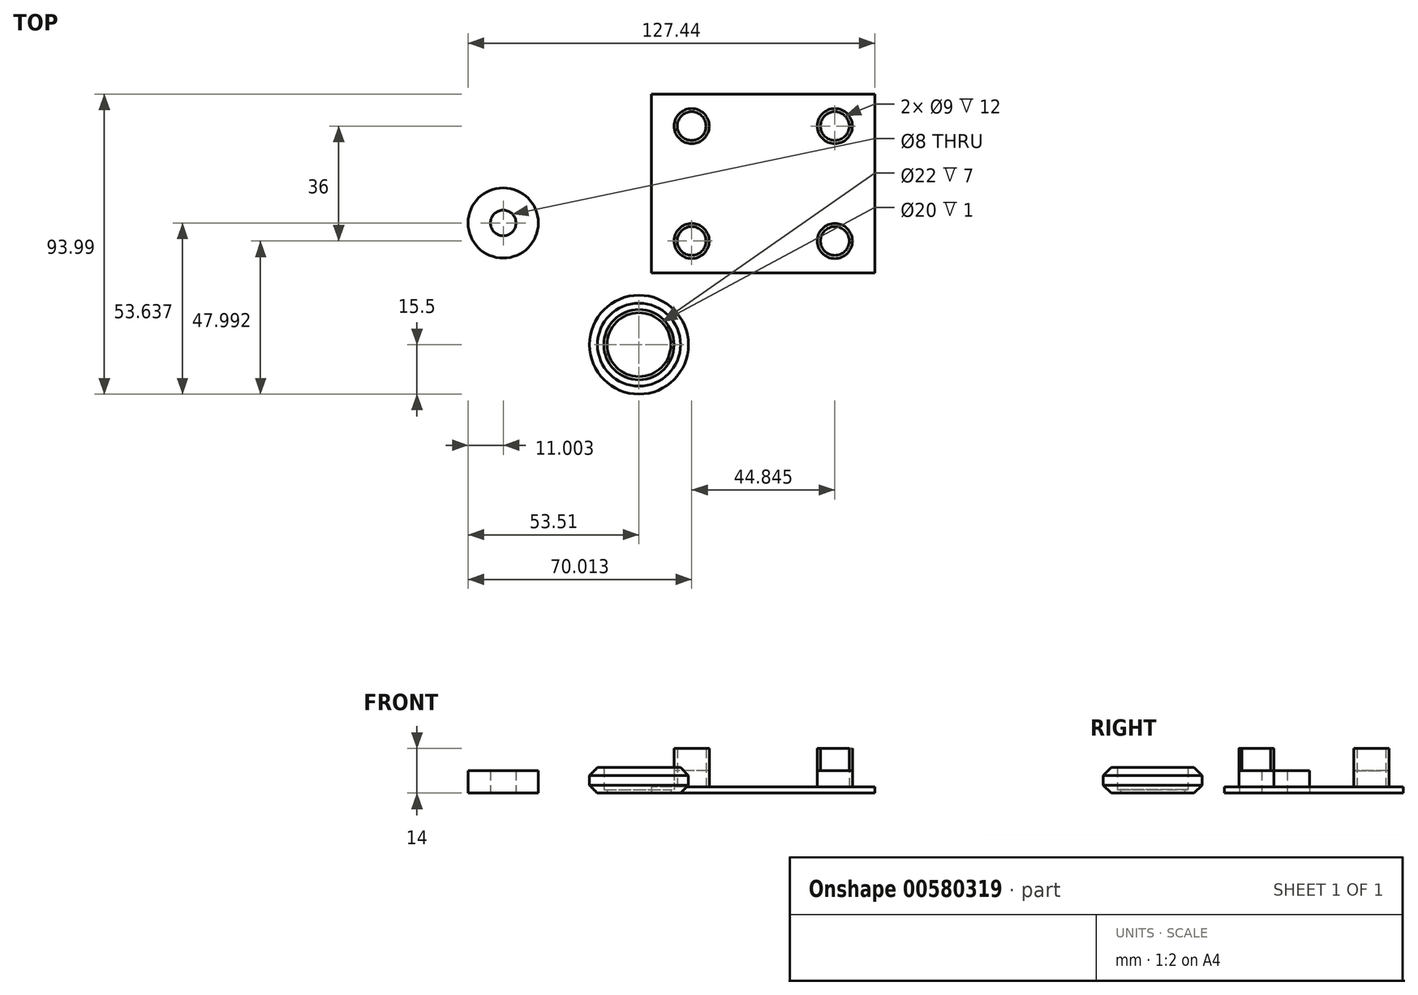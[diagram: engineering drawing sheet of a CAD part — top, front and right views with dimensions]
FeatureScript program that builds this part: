
annotation { "Feature Type Name" : "Feature", "Feature Type Description" : "" }
export const myFeature = defineFeature(function(context is Context, id is Id, definition is map)
    precondition{}
    {
        {
            var Q0;
            Q0=qCreatedBy(makeId("Right.planeOp"),FACE);
            var sketch = newSketch(context, id + "F0", { "sketchPlane" : qUnion([Q0])});
            skLineSegment(sketch, "E0", {"start": v(0, 0) * mm, "end": v(2, 0) * mm});
            skLineSegment(sketch, "E1", {"start": v(2, 0) * mm, "end": v(6, 4) * mm});
            skLineSegment(sketch, "E2", {"start": v(6, 4) * mm, "end": v(2, 8) * mm});
            skLineSegment(sketch, "E3", {"start": v(2, 8) * mm, "end": v(0, 8) * mm});
            skLineSegment(sketch, "E4", {"start": v(0, 8) * mm, "end": v(0, 0) * mm});
            skLineSegment(sketch, "E5", {"start": v(-11, 0) * mm, "end": v(-11, 5.99) * mm});
            skLineSegment(sketch, "E6.bottom", {"start": v(0, 1) * mm, "end": v(-1, 1) * mm});
            skLineSegment(sketch, "E6.top", {"start": v(0, 0) * mm, "end": v(-1, 0) * mm});
            skLineSegment(sketch, "E6.left", {"start": v(0, 1) * mm, "end": v(0, 0) * mm});
            skLineSegment(sketch, "E6.right", {"start": v(-1, 1) * mm, "end": v(-1, 0) * mm});
            skLineSegment(sketch, "E7", {"start": v(4.5, 5.5) * mm, "end": v(4.5, 2.5) * mm});
            skSolve(sketch);
        }
        {
            var Q0;
            {var subQ4=sQuery(id+"F0.wireOp",EDGE,"E0");Q0=makeQuery(id+"F0.imprint","IMPRINT",FACE,{"disambiguationData":[TD([[makeQuery(id+"F0.imprint","IMPRINT",EDGE,{"derivedFrom":subQ4}),1.0]])]});}
            var Q1;
            Q1=makeQuery(id+"F0.imprint","IMPRINT",FACE,{"disambiguationData":[TD([[makeQuery(id+"F0.imprint","IMPRINT",EDGE,{"derivedFrom":sQuery(id+"F0.wireOp",EDGE,"E6.bottom")}),1.0]])]});
            var Q2;
            Q2=sQuery(id+"F0.wireOp",EDGE,"E5");
            revolve(context, id + "F1", {"entities" : qUnion([Q0, Q1]), "axis" : qUnion([Q2]), "revolveType" : RevolveType.FULL});
        }
        {
            var Q0;
            Q0=qCreatedBy(makeId("Top.planeOp"),FACE);
            var sketch = newSketch(context, id + "F2", { "sketchPlane" : qUnion([Q0])});
            skCircle(sketch, "E8", {"center": v(-42.5, 27.14) * mm, "radius": 11 * mm});
            skCircle(sketch, "E9", {"center": v(-42.5, 27.14) * mm, "radius": 4 * mm});
            skSolve(sketch);
        }
        {
            var Q0;
            Q0=qSketchRegion(id+"F2",true);
            extrude(context, id + "F3", {"entities" : qUnion([Q0]), "depth" : 7 * mm});
        }
        {
            var Q0;
            Q0=qCreatedBy(makeId("Top.planeOp"),FACE);
            var sketch = newSketch(context, id + "F4", { "sketchPlane" : qUnion([Q0])});
            skLineSegment(sketch, "E10.bottom", {"start": v(73.93, 11.5) * mm, "end": v(3.93, 11.5) * mm});
            skLineSegment(sketch, "E10.top", {"start": v(73.93, 67.5) * mm, "end": v(3.93, 67.5) * mm});
            skLineSegment(sketch, "E10.left", {"start": v(73.93, 11.5) * mm, "end": v(73.93, 67.5) * mm});
            skLineSegment(sketch, "E10.right", {"start": v(3.93, 11.5) * mm, "end": v(3.93, 67.5) * mm});
            skSolve(sketch);
        }
        {
            var Q0;
            Q0=qSketchRegion(id+"F4",true);
            extrude(context, id + "F5", {"entities" : qUnion([Q0]), "depth" : 2 * mm});
        }
        {
            var Q0;
            Q0=makeQuery(id+"F5.opExtrude","CAP_FACE",FACE,{"disambiguationData":[OSD([sQuery(id+"F4.wireOp",EDGE,"E10.bottom"),sQuery(id+"F4.wireOp",EDGE,"E10.top"),sQuery(id+"F4.wireOp",EDGE,"E10.left"),sQuery(id+"F4.wireOp",EDGE,"E10.right")])],"isStart":false});
            var sketch = newSketch(context, id + "F6", { "sketchPlane" : qUnion([Q0])});
            skLineSegment(sketch, "E11", {"start": v(38.93, 11.5) * mm, "end": v(38.93, 67.5) * mm});
            skLineSegment(sketch, "E12", {"start": v(3.93, 39.5) * mm, "end": v(73.93, 39.5) * mm});
            skCircle(sketch, "E13", {"center": v(61.35, 21.5) * mm, "radius": 5.5 * mm});
            skCircle(sketch, "E14", {"center": v(61.35, 21.5) * mm, "radius": 4.5 * mm});
            skCircle(sketch, "E15.MirrorC", {"center": v(16.5, 21.5) * mm, "radius": 5.5 * mm});
            skCircle(sketch, "E16.MirrorC", {"center": v(16.5, 21.5) * mm, "radius": 4.5 * mm});
            skLineSegment(sketch, "E17.MirrorCS", {"start": v(73.93, 39.5) * mm, "end": v(3.93, 39.5) * mm});
            skCircle(sketch, "E18.MirrorC", {"center": v(61.35, 57.5) * mm, "radius": 4.5 * mm});
            skCircle(sketch, "E19.MirrorC", {"center": v(61.35, 57.5) * mm, "radius": 5.5 * mm});
            skCircle(sketch, "E20.MirrorC", {"center": v(16.5, 57.5) * mm, "radius": 5.5 * mm});
            skCircle(sketch, "E21.MirrorC", {"center": v(16.5, 57.5) * mm, "radius": 4.5 * mm});
            skSolve(sketch);
        }
        {
            var Q0;
            Q0=makeQuery(id+"F6.imprint","IMPRINT",FACE,{"disambiguationData":[TD([[makeQuery(id+"F6.imprint","IMPRINT",EDGE,{"derivedFrom":sQuery(id+"F6.wireOp",EDGE,"E14")}),1.0]])]});
            var Q1;
            Q1=makeQuery(id+"F6.imprint","IMPRINT",FACE,{"disambiguationData":[TD([[makeQuery(id+"F6.imprint","IMPRINT",EDGE,{"derivedFrom":sQuery(id+"F6.wireOp",EDGE,"E16.MirrorC")}),-1.0]])]});
            var Q2;
            Q2=makeQuery(id+"F6.imprint","IMPRINT",FACE,{"disambiguationData":[TD([[makeQuery(id+"F6.imprint","IMPRINT",EDGE,{"derivedFrom":sQuery(id+"F6.wireOp",EDGE,"E21.MirrorC")}),1.0]])]});
            var Q3;
            Q3=makeQuery(id+"F6.imprint","IMPRINT",FACE,{"disambiguationData":[TD([[makeQuery(id+"F6.imprint","IMPRINT",EDGE,{"derivedFrom":sQuery(id+"F6.wireOp",EDGE,"E18.MirrorC")}),-1.0]])]});
            extrude(context, id + "F7", {"entities" : qUnion([Q0, Q1, Q2, Q3]), "operationType" : NewBodyOperationType.ADD, "depth" : 12 * mm});
        }
        {
            var Q0;
            Q0=qSketchRegion(id+"F6",true);
            extrude(context, id + "F8", {"entities" : qUnion([Q0]), "operationType" : NewBodyOperationType.ADD, "depth" : 5 * mm});
        }
    });
